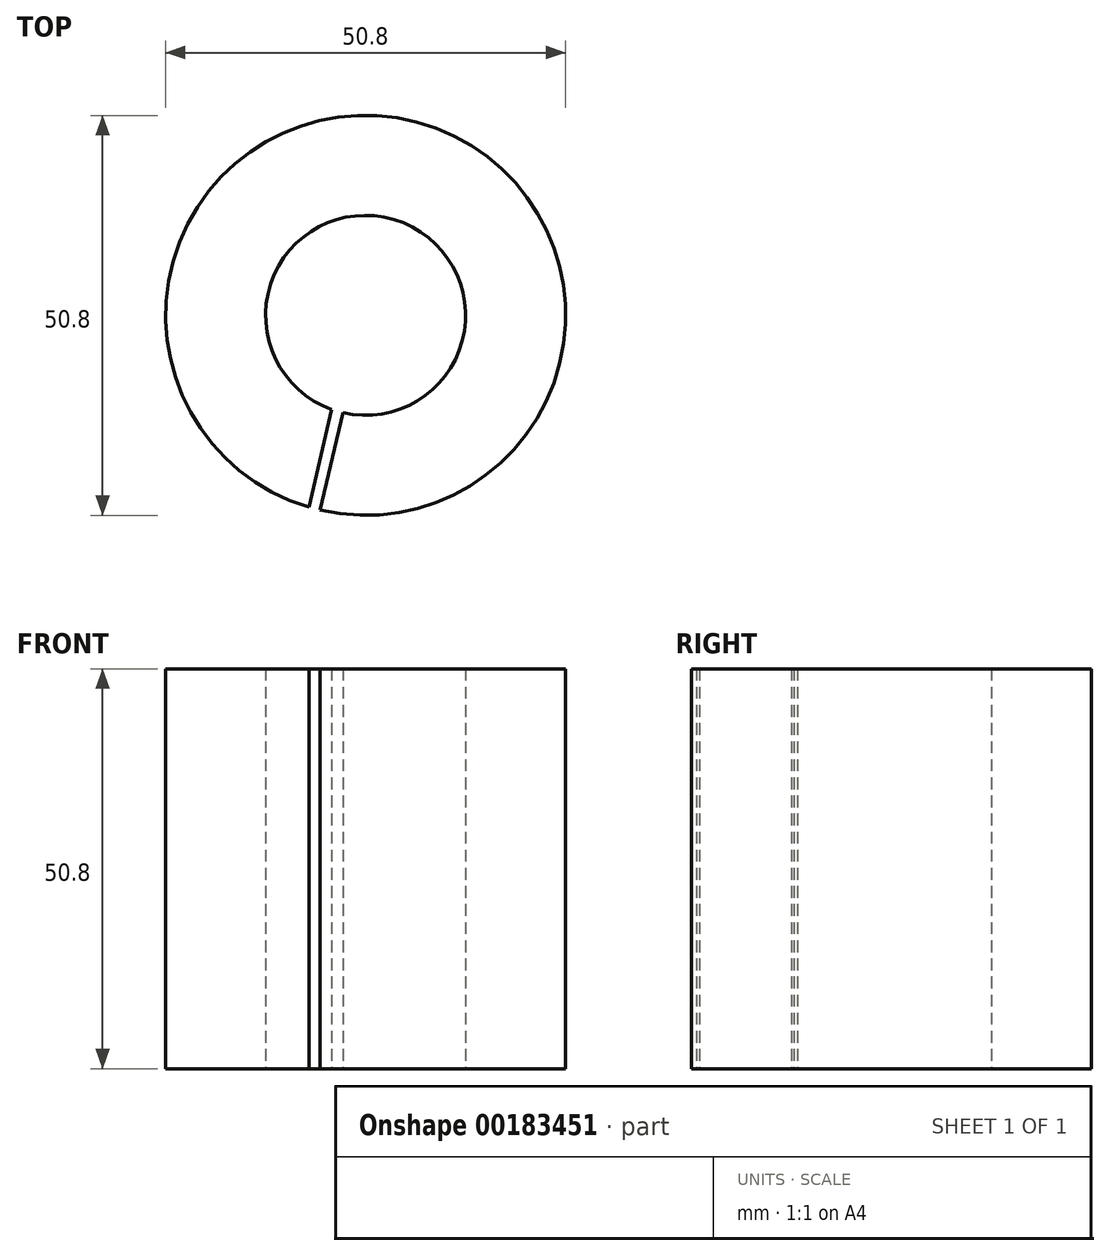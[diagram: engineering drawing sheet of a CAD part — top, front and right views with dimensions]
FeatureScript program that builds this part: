
annotation { "Feature Type Name" : "Feature", "Feature Type Description" : "" }
export const myFeature = defineFeature(function(context is Context, id is Id, definition is map)
    precondition{}
    {
        {
            var Q0;
            Q0=qCreatedBy(makeId("Top.planeOp"),FACE);
            var sketch = newSketch(context, id + "F0", { "sketchPlane" : qUnion([Q0])});
            skCircle(sketch, "E0", {"center": v(-54.27, 40) * mm, "radius": 25.4 * mm});
            skCircle(sketch, "E1", {"center": v(-54.27, 40) * mm, "radius": 12.7 * mm});
            skLineSegment(sketch, "E2", {"start": v(-58.58, 28.05) * mm, "end": v(-61.47, 15.64) * mm});
            skLineSegment(sketch, "E3", {"start": v(-57.15, 27.63) * mm, "end": v(-60.03, 15.26) * mm});
            skPoint(sketch, "E3.endSnap0", {"position": v(-60.03, 21.85) * mm});
            skSolve(sketch);
        }
        {
            var Q0;
            {var subQ0=sQuery(id+"F0.wireOp",EDGE,"E2");Q0=makeQuery(id+"F0.imprint","IMPRINT",FACE,{"disambiguationData":[TD([[makeQuery(id+"F0.imprint","IMPRINT",EDGE,{"derivedFrom":subQ0}),-1.0]])]});}
            extrude(context, id + "F1", {"entities" : qUnion([Q0]), "depth" : 50.8 * mm});
        }
    });
